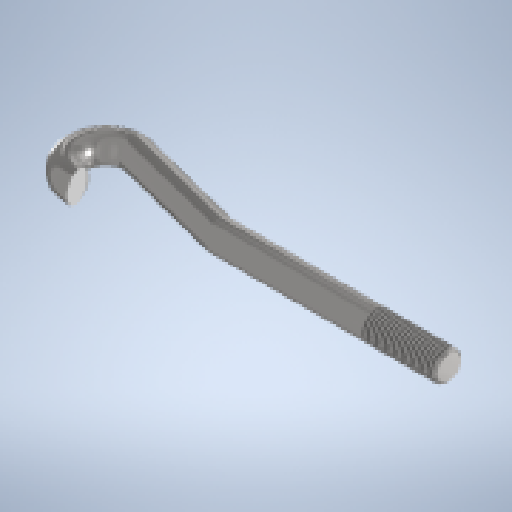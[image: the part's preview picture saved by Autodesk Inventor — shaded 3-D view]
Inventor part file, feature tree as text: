
AUTODESK INVENTOR PART (.ipt)
format: ipt  version: 2025 (Build 290162010, 162A)  size: 205,312 bytes
history: native  units: mm
features: other x3, extrude x1, sketch x1
ambient origin geometry x8: Origin, YZ Plane, XZ Plane, XY Plane, X Axis, Y Axis, Z Axis, Center Point
bodies: Solid1 (feature_tree)
feature tree (5):
  other  "DIN 529 M12 x 160"
  extrude  "Extrusion1"  Depth=5.5mm TaperAngle=0.0deg
  other  "Solid1::DIN 529 M12 x 160"
  other  "Bezeichnung1"
  sketch  "Skizze1"  dims[d0=2.5mm d1=5.5mm d2=0.0mm]
